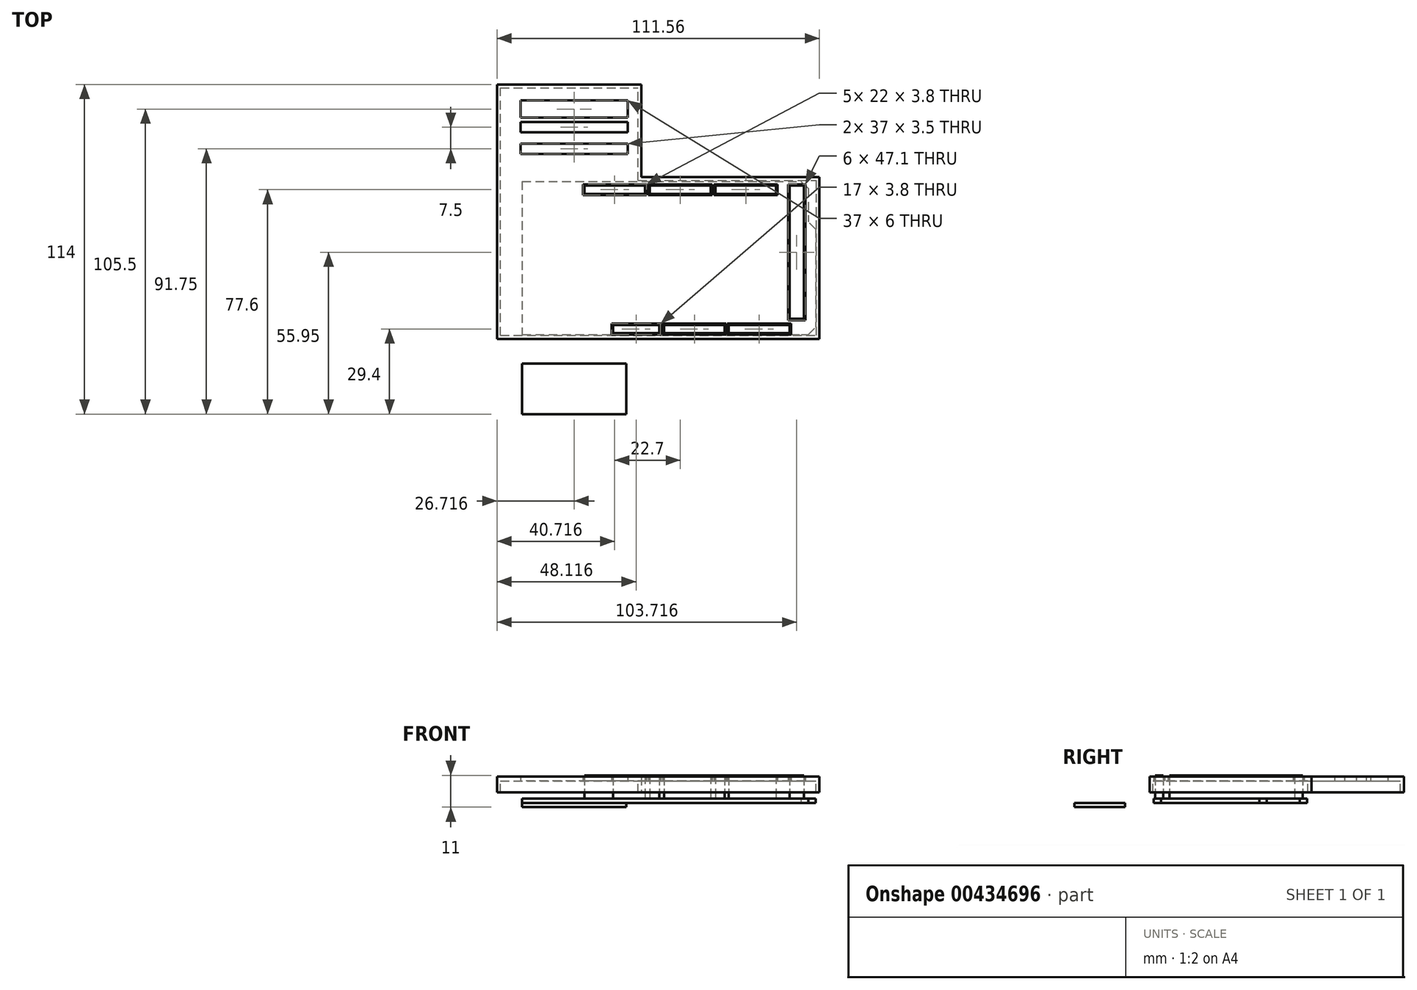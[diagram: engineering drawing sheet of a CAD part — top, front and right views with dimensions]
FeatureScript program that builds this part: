
annotation { "Feature Type Name" : "Feature", "Feature Type Description" : "" }
export const myFeature = defineFeature(function(context is Context, id is Id, definition is map)
    precondition{}
    {
        {
            var Q0;
            Q0=qCreatedBy(makeId("Top.planeOp"),FACE);
            var sketch = newSketch(context, id + "F0", { "sketchPlane" : qUnion([Q0])});
            skLineSegment(sketch, "E0", {"start": v(0, 53.02) * mm, "end": v(0, -53.02) * mm, "construction": true});
            skLineSegment(sketch, "E1", {"start": v(-65.78, 0) * mm, "end": v(65.78, 0) * mm, "construction": true});
            skLineSegment(sketch, "E2", {"start": v(-47.06, 26.5) * mm, "end": v(-47.06, -26.5) * mm});
            skLineSegment(sketch, "E3", {"start": v(54.44, 12.5) * mm, "end": v(54.44, -26.5) * mm});
            skLineSegment(sketch, "E4", {"start": v(51.94, 26.5) * mm, "end": v(51.94, 12.5) * mm});
            skLineSegment(sketch, "E5", {"start": v(-47.06, 26.5) * mm, "end": v(51.94, 26.5) * mm});
            skLineSegment(sketch, "E6", {"start": v(-47.06, -26.5) * mm, "end": v(54.44, -26.5) * mm});
            skLineSegment(sketch, "E7", {"start": v(54.44, 12.5) * mm, "end": v(51.94, 12.5) * mm});
            skSolve(sketch);
        }
        {
            var Q0;
            Q0=makeQuery(id+"F0.imprint","IMPRINT",FACE,{"disambiguationData":[TD([[makeQuery(id+"F0.imprint","IMPRINT",EDGE,{"derivedFrom":sQuery(id+"F0.wireOp",EDGE,"E2")}),1.0]])]});
            extrude(context, id + "F1", {"entities" : qUnion([Q0]), "depth" : 1.5 * mm});
        }
        {
            var Q0;
            Q0=makeQuery(id+"F1.opExtrude","SWEPT_EDGE",EDGE,{"disambiguationData":[OSD([sQuery(id+"F0.wireOp",EDGE,"E3"),sQuery(id+"F0.wireOp",EDGE,"E7")])]});
            var Q1;
            Q1=makeQuery(id+"F1.opExtrude","SWEPT_EDGE",EDGE,{"disambiguationData":[OSD([sQuery(id+"F0.wireOp",EDGE,"E4"),sQuery(id+"F0.wireOp",EDGE,"E5")])]});
            var Q2;
            Q2=makeQuery(id+"F1.opExtrude","SWEPT_EDGE",EDGE,{"disambiguationData":[OSD([sQuery(id+"F0.wireOp",EDGE,"E3"),sQuery(id+"F0.wireOp",EDGE,"E6")])]});
            chamfer(context, id + "F2", {"entities" : qUnion([Q0, Q1, Q2]), "width" : 2.5 * mm, "tangentPropagation" : true});
        }
        {
            var Q0;
            Q0=makeQuery(id+"F1.opExtrude","CAP_FACE",FACE,{"disambiguationData":[OSD([sQuery(id+"F0.wireOp",EDGE,"E2"),sQuery(id+"F0.wireOp",EDGE,"E3"),sQuery(id+"F0.wireOp",EDGE,"E4"),sQuery(id+"F0.wireOp",EDGE,"E5"),sQuery(id+"F0.wireOp",EDGE,"E6"),sQuery(id+"F0.wireOp",EDGE,"E7")])],"isStart":false});
            var sketch = newSketch(context, id + "F3", { "sketchPlane" : qUnion([Q0])});
            skLineSegment(sketch, "E8.bottom", {"start": v(45.44, 25) * mm, "end": v(50.44, 25) * mm});
            skLineSegment(sketch, "E8.top", {"start": v(45.44, -21.1) * mm, "end": v(50.44, -21.1) * mm});
            skLineSegment(sketch, "E8.left", {"start": v(45.44, 25) * mm, "end": v(45.44, -21.1) * mm});
            skLineSegment(sketch, "E8.right", {"start": v(50.44, 25) * mm, "end": v(50.44, -21.1) * mm});
            skLineSegment(sketch, "E9.0", {"start": v(-47.06, 26.5) * mm, "end": v(49.44, 26.5) * mm, "construction": true});
            skLineSegment(sketch, "E9.1", {"start": v(51.94, 24) * mm, "end": v(49.44, 26.5) * mm, "construction": true});
            skLineSegment(sketch, "E9.2", {"start": v(51.94, 24) * mm, "end": v(51.94, 12.5) * mm, "construction": true});
            skLineSegment(sketch, "E9.3", {"start": v(54.44, 10) * mm, "end": v(51.94, 12.5) * mm, "construction": true});
            skLineSegment(sketch, "E9.4", {"start": v(54.44, 10) * mm, "end": v(54.44, -24) * mm, "construction": true});
            skLineSegment(sketch, "E9.5", {"start": v(-47.06, 26.5) * mm, "end": v(-47.06, -26.5) * mm, "construction": true});
            skLineSegment(sketch, "E9.6", {"start": v(-47.06, -26.5) * mm, "end": v(51.94, -26.5) * mm, "construction": true});
            skLineSegment(sketch, "E10.bottom", {"start": v(40.84, 25) * mm, "end": v(19.84, 25) * mm});
            skLineSegment(sketch, "E10.top", {"start": v(40.84, 22.2) * mm, "end": v(19.84, 22.2) * mm});
            skLineSegment(sketch, "E10.left", {"start": v(40.84, 25) * mm, "end": v(40.84, 22.2) * mm});
            skLineSegment(sketch, "E10.right", {"start": v(19.84, 25) * mm, "end": v(19.84, 22.2) * mm});
            skLineSegment(sketch, "E11.bottom", {"start": v(18.14, 25) * mm, "end": v(-2.86, 25) * mm});
            skLineSegment(sketch, "E11.top", {"start": v(18.14, 22.2) * mm, "end": v(-2.86, 22.2) * mm});
            skLineSegment(sketch, "E11.left", {"start": v(18.14, 25) * mm, "end": v(18.14, 22.2) * mm});
            skLineSegment(sketch, "E11.right", {"start": v(-2.86, 25) * mm, "end": v(-2.86, 22.2) * mm});
            skLineSegment(sketch, "E12.bottom", {"start": v(-4.56, 25) * mm, "end": v(-25.56, 25) * mm});
            skLineSegment(sketch, "E12.top", {"start": v(-4.56, 22.2) * mm, "end": v(-25.56, 22.2) * mm});
            skLineSegment(sketch, "E12.left", {"start": v(-4.56, 25) * mm, "end": v(-4.56, 22.2) * mm});
            skLineSegment(sketch, "E12.right", {"start": v(-25.56, 25) * mm, "end": v(-25.56, 22.2) * mm});
            skLineSegment(sketch, "E13.bottom", {"start": v(45.44, -23.2) * mm, "end": v(24.44, -23.2) * mm});
            skLineSegment(sketch, "E13.top", {"start": v(45.44, -26) * mm, "end": v(24.44, -26) * mm});
            skLineSegment(sketch, "E13.left", {"start": v(45.44, -23.2) * mm, "end": v(45.44, -26) * mm});
            skLineSegment(sketch, "E13.right", {"start": v(24.44, -23.2) * mm, "end": v(24.44, -26) * mm});
            skLineSegment(sketch, "E14.bottom", {"start": v(23.04, -23.2) * mm, "end": v(2.04, -23.2) * mm});
            skLineSegment(sketch, "E14.top", {"start": v(23.04, -26) * mm, "end": v(2.04, -26) * mm});
            skLineSegment(sketch, "E14.left", {"start": v(23.04, -23.2) * mm, "end": v(23.04, -26) * mm});
            skLineSegment(sketch, "E14.right", {"start": v(2.04, -23.2) * mm, "end": v(2.04, -26) * mm});
            skLineSegment(sketch, "E15.bottom", {"start": v(0.34, -23.2) * mm, "end": v(-15.66, -23.2) * mm});
            skLineSegment(sketch, "E15.top", {"start": v(0.34, -26) * mm, "end": v(-15.66, -26) * mm});
            skLineSegment(sketch, "E15.left", {"start": v(0.34, -23.2) * mm, "end": v(0.34, -26) * mm});
            skLineSegment(sketch, "E15.right", {"start": v(-15.66, -23.2) * mm, "end": v(-15.66, -26) * mm});
            skSolve(sketch);
        }
        {
            var Q0;
            Q0=makeQuery(id+"F3.imprint","IMPRINT",FACE,{"disambiguationData":[TD([[makeQuery(id+"F3.imprint","IMPRINT",EDGE,{"derivedFrom":sQuery(id+"F3.wireOp",EDGE,"E12.bottom")}),1.0]])]});
            var Q1;
            Q1=makeQuery(id+"F3.imprint","IMPRINT",FACE,{"disambiguationData":[TD([[makeQuery(id+"F3.imprint","IMPRINT",EDGE,{"derivedFrom":sQuery(id+"F3.wireOp",EDGE,"E11.bottom")}),1.0]])]});
            var Q2;
            Q2=makeQuery(id+"F3.imprint","IMPRINT",FACE,{"disambiguationData":[TD([[makeQuery(id+"F3.imprint","IMPRINT",EDGE,{"derivedFrom":sQuery(id+"F3.wireOp",EDGE,"E10.bottom")}),1.0]])]});
            var Q3;
            Q3=makeQuery(id+"F3.imprint","IMPRINT",FACE,{"disambiguationData":[TD([[makeQuery(id+"F3.imprint","IMPRINT",EDGE,{"derivedFrom":sQuery(id+"F3.wireOp",EDGE,"E8.bottom")}),-1.0]])]});
            var Q4;
            Q4=makeQuery(id+"F3.imprint","IMPRINT",FACE,{"disambiguationData":[TD([[makeQuery(id+"F3.imprint","IMPRINT",EDGE,{"derivedFrom":sQuery(id+"F3.wireOp",EDGE,"E13.bottom")}),1.0]])]});
            var Q5;
            Q5=makeQuery(id+"F3.imprint","IMPRINT",FACE,{"disambiguationData":[TD([[makeQuery(id+"F3.imprint","IMPRINT",EDGE,{"derivedFrom":sQuery(id+"F3.wireOp",EDGE,"E14.bottom")}),1.0]])]});
            var Q6;
            Q6=makeQuery(id+"F3.imprint","IMPRINT",FACE,{"disambiguationData":[TD([[makeQuery(id+"F3.imprint","IMPRINT",EDGE,{"derivedFrom":sQuery(id+"F3.wireOp",EDGE,"E15.bottom")}),1.0]])]});
            extrude(context, id + "F4", {"entities" : qUnion([Q0, Q1, Q2, Q3, Q4, Q5, Q6]), "operationType" : NewBodyOperationType.ADD, "depth" : 8 * mm});
        }
        {
            var Q0;
            Q0=qCreatedBy(makeId("Top.planeOp"),FACE);
            var sketch = newSketch(context, id + "F5", { "sketchPlane" : qUnion([Q0])});
            skLineSegment(sketch, "E16.bottom", {"start": v(-47.06, -36.5) * mm, "end": v(-11.06, -36.5) * mm});
            skLineSegment(sketch, "E16.top", {"start": v(-47.06, -54) * mm, "end": v(-11.06, -54) * mm});
            skLineSegment(sketch, "E16.left", {"start": v(-47.06, -36.5) * mm, "end": v(-47.06, -54) * mm});
            skLineSegment(sketch, "E16.right", {"start": v(-11.06, -36.5) * mm, "end": v(-11.06, -54) * mm});
            skPoint(sketch, "E17.0", {"position": v(-47.06, -26.5) * mm});
            skLineSegment(sketch, "E18.0", {"start": v(-65.78, 0) * mm, "end": v(65.78, 0) * mm, "construction": true});
            skLineSegment(sketch, "E18.1", {"start": v(0, 53.02) * mm, "end": v(0, -53.02) * mm, "construction": true});
            skLineSegment(sketch, "E19.MirrorCS", {"start": v(-47.06, 36.5) * mm, "end": v(-47.06, 54) * mm});
            skLineSegment(sketch, "E20.MirrorCS", {"start": v(-47.06, 36.5) * mm, "end": v(-11.06, 36.5) * mm});
            skLineSegment(sketch, "E21.MirrorCS", {"start": v(-11.06, 36.5) * mm, "end": v(-11.06, 54) * mm});
            skLineSegment(sketch, "E22.MirrorCS", {"start": v(-47.06, 54) * mm, "end": v(-11.06, 54) * mm});
            skSolve(sketch);
        }
        {
            var Q0;
            Q0=makeQuery(id+"F5.imprint","IMPRINT",FACE,{"disambiguationData":[TD([[makeQuery(id+"F5.imprint","IMPRINT",EDGE,{"derivedFrom":sQuery(id+"F5.wireOp",EDGE,"E16.bottom")}),-1.0]])]});
            extrude(context, id + "F6", {"entities" : qUnion([Q0]), "oppositeDirection" : true, "depth" : 1.5 * mm});
        }
        {
            var Q0;
            Q0=makeQuery(id+"F6.opExtrude","CAP_FACE",FACE,{"disambiguationData":[OSD([sQuery(id+"F5.wireOp",EDGE,"E16.bottom"),sQuery(id+"F5.wireOp",EDGE,"E16.top"),sQuery(id+"F5.wireOp",EDGE,"E16.left"),sQuery(id+"F5.wireOp",EDGE,"E16.right")])],"isStart":false});
            var sketch = newSketch(context, id + "F7", { "sketchPlane" : qUnion([Q0])});
            skLineSegment(sketch, "E23.bottom", {"start": v(-47.06, 36.5) * mm, "end": v(-11.06, 36.5) * mm, "construction": true});
            skLineSegment(sketch, "E23.top", {"start": v(-47.06, 34) * mm, "end": v(-11.06, 34) * mm, "construction": true});
            skLineSegment(sketch, "E23.left", {"start": v(-47.06, 36.5) * mm, "end": v(-47.06, 34) * mm, "construction": true});
            skLineSegment(sketch, "E23.right", {"start": v(-11.06, 36.5) * mm, "end": v(-11.06, 34) * mm, "construction": true});
            skLineSegment(sketch, "E24.bottom", {"start": v(-47.06, 54) * mm, "end": v(-11.06, 54) * mm, "construction": true});
            skLineSegment(sketch, "E24.top", {"start": v(-47.06, 56.5) * mm, "end": v(-11.06, 56.5) * mm, "construction": true});
            skLineSegment(sketch, "E24.left", {"start": v(-47.06, 54) * mm, "end": v(-47.06, 56.5) * mm, "construction": true});
            skLineSegment(sketch, "E24.right", {"start": v(-11.06, 54) * mm, "end": v(-11.06, 56.5) * mm, "construction": true});
            skLineSegment(sketch, "E25.0", {"start": v(-47.06, -36.5) * mm, "end": v(-47.06, -39) * mm});
            skLineSegment(sketch, "E25.1", {"start": v(-47.06, -54) * mm, "end": v(-11.06, -54) * mm});
            skLineSegment(sketch, "E25.2", {"start": v(-11.06, -36.5) * mm, "end": v(-11.06, -39) * mm});
            skLineSegment(sketch, "E25.3", {"start": v(-47.06, -36.5) * mm, "end": v(-11.06, -36.5) * mm});
            skLineSegment(sketch, "E26", {"start": v(-47.06, -39) * mm, "end": v(-11.06, -39) * mm});
            skLineSegment(sketch, "E27", {"start": v(-47.06, -45.25) * mm, "end": v(-11.06, -45.25) * mm, "construction": true});
            skLineSegment(sketch, "E28.MirrorCS", {"start": v(-47.06, -51.5) * mm, "end": v(-11.06, -51.5) * mm});
            skLineSegment(sketch, "E29", {"start": v(-47.06, -39) * mm, "end": v(-47.06, -44) * mm});
            skLineSegment(sketch, "E30", {"start": v(-47.06, -51.5) * mm, "end": v(-47.06, -54) * mm});
            skLineSegment(sketch, "E31", {"start": v(-11.06, -51.5) * mm, "end": v(-11.06, -54) * mm});
            skLineSegment(sketch, "E32", {"start": v(-11.06, -39) * mm, "end": v(-11.06, -44) * mm});
            skLineSegment(sketch, "E33", {"start": v(-47.06, -49) * mm, "end": v(-11.06, -49) * mm});
            skLineSegment(sketch, "E34", {"start": v(-11.06, -46.5) * mm, "end": v(-47.06, -46.5) * mm});
            skLineSegment(sketch, "E35", {"start": v(-47.06, -44) * mm, "end": v(-11.06, -44) * mm});
            skLineSegment(sketch, "E36", {"start": v(-47.06, -49) * mm, "end": v(-47.06, -51.5) * mm});
            skLineSegment(sketch, "E37", {"start": v(-47.06, -46.5) * mm, "end": v(-47.06, -49) * mm});
            skLineSegment(sketch, "E38", {"start": v(-47.06, -44) * mm, "end": v(-47.06, -46.5) * mm});
            skLineSegment(sketch, "E39", {"start": v(-11.06, -49) * mm, "end": v(-11.06, -51.5) * mm});
            skLineSegment(sketch, "E40", {"start": v(-11.06, -46.5) * mm, "end": v(-11.06, -49) * mm});
            skLineSegment(sketch, "E41", {"start": v(-11.06, -44) * mm, "end": v(-11.06, -46.5) * mm});
            skSolve(sketch);
        }
        {
            var Q0;
            Q0=qCreatedBy(makeId("Top.planeOp"),FACE);
            cPlane(context, id + "F8", {"entities" : qUnion([Q0]), "cplaneType" : CPlaneType.OFFSET, "offset" : 7.6 * mm, "width" : 150 * mm, "height" : 150 * mm});
        }
        {
            var Q0;
            Q0=qCreatedBy(id+"F8.planeOp",FACE);
            var sketch = newSketch(context, id + "F9", { "sketchPlane" : qUnion([Q0])});
            skLineSegment(sketch, "E42.0.0", {"start": v(-25.56, 22.2) * mm, "end": v(-4.56, 22.2) * mm, "construction": true});
            skLineSegment(sketch, "E42.0.1", {"start": v(-4.56, 22.2) * mm, "end": v(-4.56, 25) * mm, "construction": true});
            skLineSegment(sketch, "E42.0.2", {"start": v(-4.56, 25) * mm, "end": v(-25.56, 25) * mm, "construction": true});
            skLineSegment(sketch, "E42.0.3", {"start": v(-25.56, 25) * mm, "end": v(-25.56, 22.2) * mm, "construction": true});
            skLineSegment(sketch, "E42.1.0", {"start": v(-2.86, 22.2) * mm, "end": v(18.14, 22.2) * mm, "construction": true});
            skLineSegment(sketch, "E42.1.1", {"start": v(18.14, 22.2) * mm, "end": v(18.14, 25) * mm, "construction": true});
            skLineSegment(sketch, "E42.1.2", {"start": v(18.14, 25) * mm, "end": v(-2.86, 25) * mm, "construction": true});
            skLineSegment(sketch, "E42.1.3", {"start": v(-2.86, 25) * mm, "end": v(-2.86, 22.2) * mm, "construction": true});
            skLineSegment(sketch, "E42.2.0", {"start": v(19.84, 22.2) * mm, "end": v(40.84, 22.2) * mm, "construction": true});
            skLineSegment(sketch, "E42.2.1", {"start": v(40.84, 22.2) * mm, "end": v(40.84, 25) * mm, "construction": true});
            skLineSegment(sketch, "E42.2.2", {"start": v(40.84, 25) * mm, "end": v(19.84, 25) * mm, "construction": true});
            skLineSegment(sketch, "E42.2.3", {"start": v(19.84, 25) * mm, "end": v(19.84, 22.2) * mm, "construction": true});
            skLineSegment(sketch, "E42.3.0", {"start": v(45.44, 25) * mm, "end": v(45.44, -21.1) * mm, "construction": true});
            skLineSegment(sketch, "E42.3.1", {"start": v(45.44, -21.1) * mm, "end": v(50.44, -21.1) * mm, "construction": true});
            skLineSegment(sketch, "E42.3.2", {"start": v(50.44, -21.1) * mm, "end": v(50.44, 25) * mm, "construction": true});
            skLineSegment(sketch, "E42.3.3", {"start": v(50.44, 25) * mm, "end": v(45.44, 25) * mm, "construction": true});
            skLineSegment(sketch, "E42.4.0", {"start": v(24.44, -26) * mm, "end": v(45.44, -26) * mm, "construction": true});
            skLineSegment(sketch, "E42.4.1", {"start": v(45.44, -26) * mm, "end": v(45.44, -23.2) * mm, "construction": true});
            skLineSegment(sketch, "E42.4.2", {"start": v(45.44, -23.2) * mm, "end": v(24.44, -23.2) * mm, "construction": true});
            skLineSegment(sketch, "E42.4.3", {"start": v(24.44, -23.2) * mm, "end": v(24.44, -26) * mm, "construction": true});
            skLineSegment(sketch, "E42.5.0", {"start": v(2.04, -26) * mm, "end": v(23.04, -26) * mm, "construction": true});
            skLineSegment(sketch, "E42.5.1", {"start": v(23.04, -26) * mm, "end": v(23.04, -23.2) * mm, "construction": true});
            skLineSegment(sketch, "E42.5.2", {"start": v(23.04, -23.2) * mm, "end": v(2.04, -23.2) * mm, "construction": true});
            skLineSegment(sketch, "E42.5.3", {"start": v(2.04, -23.2) * mm, "end": v(2.04, -26) * mm, "construction": true});
            skLineSegment(sketch, "E42.6.0", {"start": v(-15.66, -26) * mm, "end": v(0.34, -26) * mm, "construction": true});
            skLineSegment(sketch, "E42.6.1", {"start": v(0.34, -26) * mm, "end": v(0.34, -23.2) * mm, "construction": true});
            skLineSegment(sketch, "E42.6.2", {"start": v(0.34, -23.2) * mm, "end": v(-15.66, -23.2) * mm, "construction": true});
            skLineSegment(sketch, "E42.6.3", {"start": v(-15.66, -23.2) * mm, "end": v(-15.66, -26) * mm, "construction": true});
            skLineSegment(sketch, "E43.0", {"start": v(-4.06, 25.5) * mm, "end": v(-26.06, 25.5) * mm});
            skLineSegment(sketch, "E43.1", {"start": v(-4.06, 21.7) * mm, "end": v(-4.06, 25.5) * mm});
            skLineSegment(sketch, "E43.2", {"start": v(-26.06, 21.7) * mm, "end": v(-4.06, 21.7) * mm});
            skLineSegment(sketch, "E43.3", {"start": v(-26.06, 25.5) * mm, "end": v(-26.06, 21.7) * mm});
            skLineSegment(sketch, "E44.0", {"start": v(-3.36, 25.5) * mm, "end": v(-3.36, 21.7) * mm});
            skLineSegment(sketch, "E44.1", {"start": v(18.64, 25.5) * mm, "end": v(-3.36, 25.5) * mm});
            skLineSegment(sketch, "E44.2", {"start": v(18.64, 21.7) * mm, "end": v(18.64, 25.5) * mm});
            skLineSegment(sketch, "E44.3", {"start": v(-3.36, 21.7) * mm, "end": v(18.64, 21.7) * mm});
            skLineSegment(sketch, "E45.0", {"start": v(41.34, 25.5) * mm, "end": v(19.34, 25.5) * mm});
            skLineSegment(sketch, "E45.1", {"start": v(41.34, 21.7) * mm, "end": v(41.34, 25.5) * mm});
            skLineSegment(sketch, "E45.2", {"start": v(19.34, 21.7) * mm, "end": v(41.34, 21.7) * mm});
            skLineSegment(sketch, "E45.3", {"start": v(19.34, 25.5) * mm, "end": v(19.34, 21.7) * mm});
            skLineSegment(sketch, "E46.0", {"start": v(50.94, 25.5) * mm, "end": v(44.94, 25.5) * mm});
            skLineSegment(sketch, "E46.1", {"start": v(50.94, -21.6) * mm, "end": v(50.94, 25.5) * mm});
            skLineSegment(sketch, "E46.2", {"start": v(44.94, -21.6) * mm, "end": v(50.94, -21.6) * mm});
            skLineSegment(sketch, "E46.3", {"start": v(44.94, 25.5) * mm, "end": v(44.94, -21.6) * mm});
            skLineSegment(sketch, "E47.0", {"start": v(45.94, -22.7) * mm, "end": v(23.94, -22.7) * mm});
            skLineSegment(sketch, "E47.1", {"start": v(45.94, -26.5) * mm, "end": v(45.94, -22.7) * mm});
            skLineSegment(sketch, "E47.2", {"start": v(23.94, -26.5) * mm, "end": v(45.94, -26.5) * mm});
            skLineSegment(sketch, "E47.3", {"start": v(23.94, -22.7) * mm, "end": v(23.94, -26.5) * mm});
            skLineSegment(sketch, "E48.0", {"start": v(23.54, -22.7) * mm, "end": v(1.54, -22.7) * mm});
            skLineSegment(sketch, "E48.1", {"start": v(23.54, -26.5) * mm, "end": v(23.54, -22.7) * mm});
            skLineSegment(sketch, "E48.2", {"start": v(1.54, -26.5) * mm, "end": v(23.54, -26.5) * mm});
            skLineSegment(sketch, "E48.3", {"start": v(1.54, -22.7) * mm, "end": v(1.54, -26.5) * mm});
            skLineSegment(sketch, "E49.0", {"start": v(0.84, -22.7) * mm, "end": v(-16.16, -22.7) * mm});
            skLineSegment(sketch, "E49.1", {"start": v(0.84, -26.5) * mm, "end": v(0.84, -22.7) * mm});
            skLineSegment(sketch, "E49.2", {"start": v(-16.16, -26.5) * mm, "end": v(0.84, -26.5) * mm});
            skLineSegment(sketch, "E49.3", {"start": v(-16.16, -22.7) * mm, "end": v(-16.16, -26.5) * mm});
            skLineSegment(sketch, "E50", {"start": v(-79.02, 0) * mm, "end": v(79.02, 0) * mm, "construction": true});
            skLineSegment(sketch, "E51", {"start": v(0, 52.1) * mm, "end": v(0, -52.1) * mm, "construction": true});
            skLineSegment(sketch, "E52.bottom", {"start": v(-55.78, 28) * mm, "end": v(-5.78, 28) * mm, "construction": true});
            skLineSegment(sketch, "E52.top", {"start": v(-55.78, -28) * mm, "end": v(-5.78, -28) * mm});
            skLineSegment(sketch, "E52.left", {"start": v(-55.78, 28) * mm, "end": v(-55.78, -28) * mm});
            skLineSegment(sketch, "E52.right", {"start": v(55.78, 28) * mm, "end": v(55.78, -28) * mm});
            skLineSegment(sketch, "E53.top", {"start": v(-55.78, -60) * mm, "end": v(-5.78, -60) * mm, "construction": true});
            skLineSegment(sketch, "E53.left", {"start": v(-55.78, -28) * mm, "end": v(-55.78, -60) * mm, "construction": true});
            skLineSegment(sketch, "E53.right", {"start": v(-5.78, -28) * mm, "end": v(-5.78, -60) * mm, "construction": true});
            skLineSegment(sketch, "E54", {"start": v(-5.78, -28) * mm, "end": v(55.78, -28) * mm});
            skLineSegment(sketch, "E55.0", {"start": v(-47.06, -34) * mm, "end": v(-11.06, -34) * mm, "construction": true});
            skLineSegment(sketch, "E55.1", {"start": v(-47.06, -36.5) * mm, "end": v(-11.06, -36.5) * mm, "construction": true});
            skLineSegment(sketch, "E55.2", {"start": v(-11.06, -36.5) * mm, "end": v(-11.06, -34) * mm, "construction": true});
            skLineSegment(sketch, "E55.3", {"start": v(-47.06, -36.5) * mm, "end": v(-47.06, -34) * mm, "construction": true});
            skLineSegment(sketch, "E55.4", {"start": v(-47.06, -54) * mm, "end": v(-47.06, -56.5) * mm, "construction": true});
            skLineSegment(sketch, "E55.5", {"start": v(-47.06, -54) * mm, "end": v(-11.06, -54) * mm, "construction": true});
            skLineSegment(sketch, "E55.6", {"start": v(-47.06, -56.5) * mm, "end": v(-11.06, -56.5) * mm, "construction": true});
            skLineSegment(sketch, "E55.7", {"start": v(-11.06, -54) * mm, "end": v(-11.06, -56.5) * mm, "construction": true});
            skLineSegment(sketch, "E56.MirrorCS", {"start": v(-5.78, 28) * mm, "end": v(-5.78, 60) * mm});
            skLineSegment(sketch, "E57.MirrorCS", {"start": v(-55.78, 60) * mm, "end": v(-5.78, 60) * mm});
            skLineSegment(sketch, "E58.MirrorCS", {"start": v(-55.78, 28) * mm, "end": v(-55.78, 60) * mm});
            skLineSegment(sketch, "E59.0", {"start": v(-47.56, -37) * mm, "end": v(-10.56, -37) * mm, "construction": true});
            skLineSegment(sketch, "E59.1", {"start": v(-47.56, -37) * mm, "end": v(-47.56, -33.5) * mm, "construction": true});
            skLineSegment(sketch, "E59.2", {"start": v(-47.56, -33.5) * mm, "end": v(-10.56, -33.5) * mm, "construction": true});
            skLineSegment(sketch, "E59.3", {"start": v(-10.56, -37) * mm, "end": v(-10.56, -33.5) * mm, "construction": true});
            skLineSegment(sketch, "E60.0", {"start": v(-52.06, -31.5) * mm, "end": v(-52.06, -59) * mm});
            skLineSegment(sketch, "E60.1", {"start": v(-6.06, -31.5) * mm, "end": v(-52.06, -31.5) * mm});
            skLineSegment(sketch, "E60.2", {"start": v(-6.06, -59) * mm, "end": v(-6.06, -31.5) * mm});
            skLineSegment(sketch, "E60.3", {"start": v(-52.06, -59) * mm, "end": v(-6.06, -59) * mm});
            skLineSegment(sketch, "E61.0", {"start": v(-47.56, -53.5) * mm, "end": v(-10.56, -53.5) * mm, "construction": true});
            skLineSegment(sketch, "E61.1", {"start": v(-47.56, -53.5) * mm, "end": v(-47.56, -57) * mm, "construction": true});
            skLineSegment(sketch, "E61.2", {"start": v(-47.56, -57) * mm, "end": v(-10.56, -57) * mm, "construction": true});
            skLineSegment(sketch, "E61.3", {"start": v(-10.56, -53.5) * mm, "end": v(-10.56, -57) * mm, "construction": true});
            skLineSegment(sketch, "E62", {"start": v(-5.78, 28) * mm, "end": v(55.78, 28) * mm});
            skLineSegment(sketch, "E63.0", {"start": v(-47.06, 54) * mm, "end": v(-11.06, 54) * mm, "construction": true});
            skLineSegment(sketch, "E63.1", {"start": v(-11.06, 51.5) * mm, "end": v(-11.06, 54) * mm, "construction": true});
            skLineSegment(sketch, "E63.2", {"start": v(-47.06, 51.5) * mm, "end": v(-11.06, 51.5) * mm, "construction": true});
            skLineSegment(sketch, "E63.3", {"start": v(-11.06, 49) * mm, "end": v(-11.06, 51.5) * mm, "construction": true});
            skLineSegment(sketch, "E63.4", {"start": v(-47.06, 49) * mm, "end": v(-11.06, 49) * mm, "construction": true});
            skLineSegment(sketch, "E63.5", {"start": v(-11.06, 46.5) * mm, "end": v(-47.06, 46.5) * mm, "construction": true});
            skLineSegment(sketch, "E63.6", {"start": v(-11.06, 44) * mm, "end": v(-11.06, 46.5) * mm, "construction": true});
            skLineSegment(sketch, "E63.7", {"start": v(-47.06, 44) * mm, "end": v(-11.06, 44) * mm, "construction": true});
            skLineSegment(sketch, "E63.8", {"start": v(-47.06, 39) * mm, "end": v(-11.06, 39) * mm, "construction": true});
            skLineSegment(sketch, "E63.9", {"start": v(-47.06, 36.5) * mm, "end": v(-47.06, 39) * mm, "construction": true});
            skLineSegment(sketch, "E63.10", {"start": v(-47.06, 44) * mm, "end": v(-47.06, 46.5) * mm, "construction": true});
            skLineSegment(sketch, "E63.11", {"start": v(-47.06, 49) * mm, "end": v(-47.06, 51.5) * mm, "construction": true});
            skLineSegment(sketch, "E63.12", {"start": v(-47.06, 51.5) * mm, "end": v(-47.06, 54) * mm, "construction": true});
            skLineSegment(sketch, "E63.13", {"start": v(-47.06, 36.5) * mm, "end": v(-11.06, 36.5) * mm, "construction": true});
            skLineSegment(sketch, "E63.14", {"start": v(-11.06, 36.5) * mm, "end": v(-11.06, 39) * mm, "construction": true});
            skLineSegment(sketch, "E64.0", {"start": v(-47.56, 51.5) * mm, "end": v(-47.56, 54.5) * mm});
            skLineSegment(sketch, "E64.1", {"start": v(-10.56, 51.5) * mm, "end": v(-10.56, 54.5) * mm});
            skLineSegment(sketch, "E64.2", {"start": v(-10.56, 48.5) * mm, "end": v(-10.56, 51.5) * mm});
            skLineSegment(sketch, "E64.3", {"start": v(-47.56, 54.5) * mm, "end": v(-10.56, 54.5) * mm});
            skLineSegment(sketch, "E64.4", {"start": v(-47.56, 48.5) * mm, "end": v(-10.56, 48.5) * mm});
            skLineSegment(sketch, "E64.5", {"start": v(-47.56, 48.5) * mm, "end": v(-47.56, 51.5) * mm});
            skLineSegment(sketch, "E65.0", {"start": v(-10.56, 47) * mm, "end": v(-47.56, 47) * mm});
            skLineSegment(sketch, "E65.1", {"start": v(-10.56, 43.5) * mm, "end": v(-10.56, 47) * mm});
            skLineSegment(sketch, "E65.2", {"start": v(-47.56, 43.5) * mm, "end": v(-10.56, 43.5) * mm});
            skLineSegment(sketch, "E65.3", {"start": v(-47.56, 43.5) * mm, "end": v(-47.56, 47) * mm});
            skLineSegment(sketch, "E66.0", {"start": v(-47.56, 39.5) * mm, "end": v(-10.56, 39.5) * mm});
            skLineSegment(sketch, "E66.1", {"start": v(-47.56, 36) * mm, "end": v(-47.56, 39.5) * mm});
            skLineSegment(sketch, "E66.2", {"start": v(-47.56, 36) * mm, "end": v(-10.56, 36) * mm});
            skLineSegment(sketch, "E66.3", {"start": v(-10.56, 36) * mm, "end": v(-10.56, 39.5) * mm});
            skSolve(sketch);
        }
        {
            var Q0;
            Q0=makeQuery(id+"F9.imprint","IMPRINT",FACE,{"disambiguationData":[TD([[makeQuery(id+"F9.imprint","IMPRINT",EDGE,{"derivedFrom":sQuery(id+"F9.wireOp",EDGE,"E43.0")}),-1.0]])]});
            var Q1;
            Q1=makeQuery(id+"F9.imprint","IMPRINT",FACE,{"disambiguationData":[TD([[makeQuery(id+"F9.imprint","IMPRINT",EDGE,{"derivedFrom":sQuery(id+"F9.wireOp",EDGE,"E53.bottom")}),-1.0]])]});
            var Q2;
            Q2=makeQuery(id+"F9.imprint","IMPRINT",FACE,{"disambiguationData":[TD([[makeQuery(id+"F9.imprint","IMPRINT",EDGE,{"derivedFrom":sQuery(id+"F9.wireOp",EDGE,"E59.0")}),-1.0]])]});
            extrude(context, id + "F10", {"entities" : qUnion([Q0, Q1, Q2]), "depth" : 1.5 * mm});
        }
        {
            var Q0;
            Q0=makeQuery(id+"F10.opExtrude","CAP_FACE",FACE,{"disambiguationData":[OSD([sQuery(id+"F9.wireOp",EDGE,"E43.0"),sQuery(id+"F9.wireOp",EDGE,"E43.1"),sQuery(id+"F9.wireOp",EDGE,"E43.2"),sQuery(id+"F9.wireOp",EDGE,"E43.3"),sQuery(id+"F9.wireOp",EDGE,"E44.0"),sQuery(id+"F9.wireOp",EDGE,"E44.1"),sQuery(id+"F9.wireOp",EDGE,"E44.2"),sQuery(id+"F9.wireOp",EDGE,"E44.3"),sQuery(id+"F9.wireOp",EDGE,"E45.0"),sQuery(id+"F9.wireOp",EDGE,"E45.1"),sQuery(id+"F9.wireOp",EDGE,"E45.2"),sQuery(id+"F9.wireOp",EDGE,"E45.3"),sQuery(id+"F9.wireOp",EDGE,"E46.0"),sQuery(id+"F9.wireOp",EDGE,"E46.1"),sQuery(id+"F9.wireOp",EDGE,"E46.2"),sQuery(id+"F9.wireOp",EDGE,"E46.3"),sQuery(id+"F9.wireOp",EDGE,"E47.0"),sQuery(id+"F9.wireOp",EDGE,"E47.1"),sQuery(id+"F9.wireOp",EDGE,"E47.2"),sQuery(id+"F9.wireOp",EDGE,"E47.3"),sQuery(id+"F9.wireOp",EDGE,"E48.0"),sQuery(id+"F9.wireOp",EDGE,"E48.1"),sQuery(id+"F9.wireOp",EDGE,"E48.2"),sQuery(id+"F9.wireOp",EDGE,"E48.3"),sQuery(id+"F9.wireOp",EDGE,"E49.0"),sQuery(id+"F9.wireOp",EDGE,"E49.1"),sQuery(id+"F9.wireOp",EDGE,"E49.2"),sQuery(id+"F9.wireOp",EDGE,"E49.3"),sQuery(id+"F9.wireOp",EDGE,"E52.bottom"),sQuery(id+"F9.wireOp",EDGE,"E52.left"),sQuery(id+"F9.wireOp",EDGE,"E52.right"),sQuery(id+"F9.wireOp",EDGE,"E53.top"),sQuery(id+"F9.wireOp",EDGE,"E53.left"),sQuery(id+"F9.wireOp",EDGE,"E53.right"),sQuery(id+"F9.wireOp",EDGE,"E54")])],"isStart":true});
            var sketch = newSketch(context, id + "F11", { "sketchPlane" : qUnion([Q0])});
            skLineSegment(sketch, "E67.0", {"start": v(-55.78, 28) * mm, "end": v(-55.78, 60) * mm, "construction": true});
            skLineSegment(sketch, "E67.1", {"start": v(-55.78, -28) * mm, "end": v(-55.78, 28) * mm});
            skLineSegment(sketch, "E67.2", {"start": v(-55.78, 60) * mm, "end": v(-5.78, 60) * mm, "construction": true});
            skLineSegment(sketch, "E67.3", {"start": v(-5.78, 28) * mm, "end": v(-5.78, 60) * mm, "construction": true});
            skLineSegment(sketch, "E67.4", {"start": v(-5.78, 28) * mm, "end": v(55.78, 28) * mm});
            skLineSegment(sketch, "E67.5", {"start": v(55.78, -28) * mm, "end": v(55.78, 28) * mm});
            skLineSegment(sketch, "E67.6", {"start": v(-55.78, -28) * mm, "end": v(-5.78, -28) * mm, "construction": true});
            skLineSegment(sketch, "E68.0", {"start": v(-54.58, -26.8) * mm, "end": v(-54.58, 30) * mm, "construction": true});
            skLineSegment(sketch, "E68.1", {"start": v(-54.58, -26.8) * mm, "end": v(54.58, -26.8) * mm, "construction": true});
            skLineSegment(sketch, "E68.2", {"start": v(-54.58, 58.8) * mm, "end": v(-6.98, 58.8) * mm, "construction": true});
            skLineSegment(sketch, "E68.3", {"start": v(-6.98, 26.8) * mm, "end": v(-6.98, 58.8) * mm, "construction": true});
            skLineSegment(sketch, "E68.4", {"start": v(-6.98, 26.8) * mm, "end": v(54.58, 26.8) * mm, "construction": true});
            skLineSegment(sketch, "E68.5", {"start": v(-54.58, 30) * mm, "end": v(-54.58, 58.8) * mm, "construction": true});
            skLineSegment(sketch, "E68.6", {"start": v(54.58, -26.8) * mm, "end": v(54.58, 26.8) * mm, "construction": true});
            skLineSegment(sketch, "E69.0", {"start": v(-54.58, -30) * mm, "end": v(-54.58, 26.8) * mm});
            skLineSegment(sketch, "E69.1", {"start": v(-54.58, -30) * mm, "end": v(-54.58, -58.8) * mm});
            skLineSegment(sketch, "E69.2", {"start": v(-54.58, 26.8) * mm, "end": v(-6, 26.8) * mm});
            skLineSegment(sketch, "E69.3", {"start": v(-54.58, -58.8) * mm, "end": v(-6.98, -58.8) * mm});
            skLineSegment(sketch, "E69.4", {"start": v(-6, 26.8) * mm, "end": v(54.58, 26.8) * mm});
            skLineSegment(sketch, "E69.5", {"start": v(54.58, -26.8) * mm, "end": v(54.58, 26.8) * mm});
            skLineSegment(sketch, "E69.6", {"start": v(-6.98, -26.8) * mm, "end": v(54.58, -26.8) * mm});
            skLineSegment(sketch, "E69.7", {"start": v(-6.98, -26.8) * mm, "end": v(-6.98, -58.8) * mm});
            skLineSegment(sketch, "E70.2", {"start": v(-5.78, -28) * mm, "end": v(55.78, -28) * mm});
            skLineSegment(sketch, "E70.3", {"start": v(-5.78, -28) * mm, "end": v(-5.78, -60) * mm});
            skLineSegment(sketch, "E70.4", {"start": v(-55.78, -60) * mm, "end": v(-5.78, -60) * mm});
            skLineSegment(sketch, "E70.5", {"start": v(-55.78, -28) * mm, "end": v(-55.78, -60) * mm});
            skLineSegment(sketch, "E70.7", {"start": v(-55.78, 28) * mm, "end": v(-5.78, 28) * mm});
            skSolve(sketch);
        }
        {
            var Q0;
            Q0=qSketchRegion(id+"F11",true);
            extrude(context, id + "F12", {"entities" : qUnion([Q0]), "operationType" : NewBodyOperationType.ADD, "depth" : 4 * mm});
        }
    });
